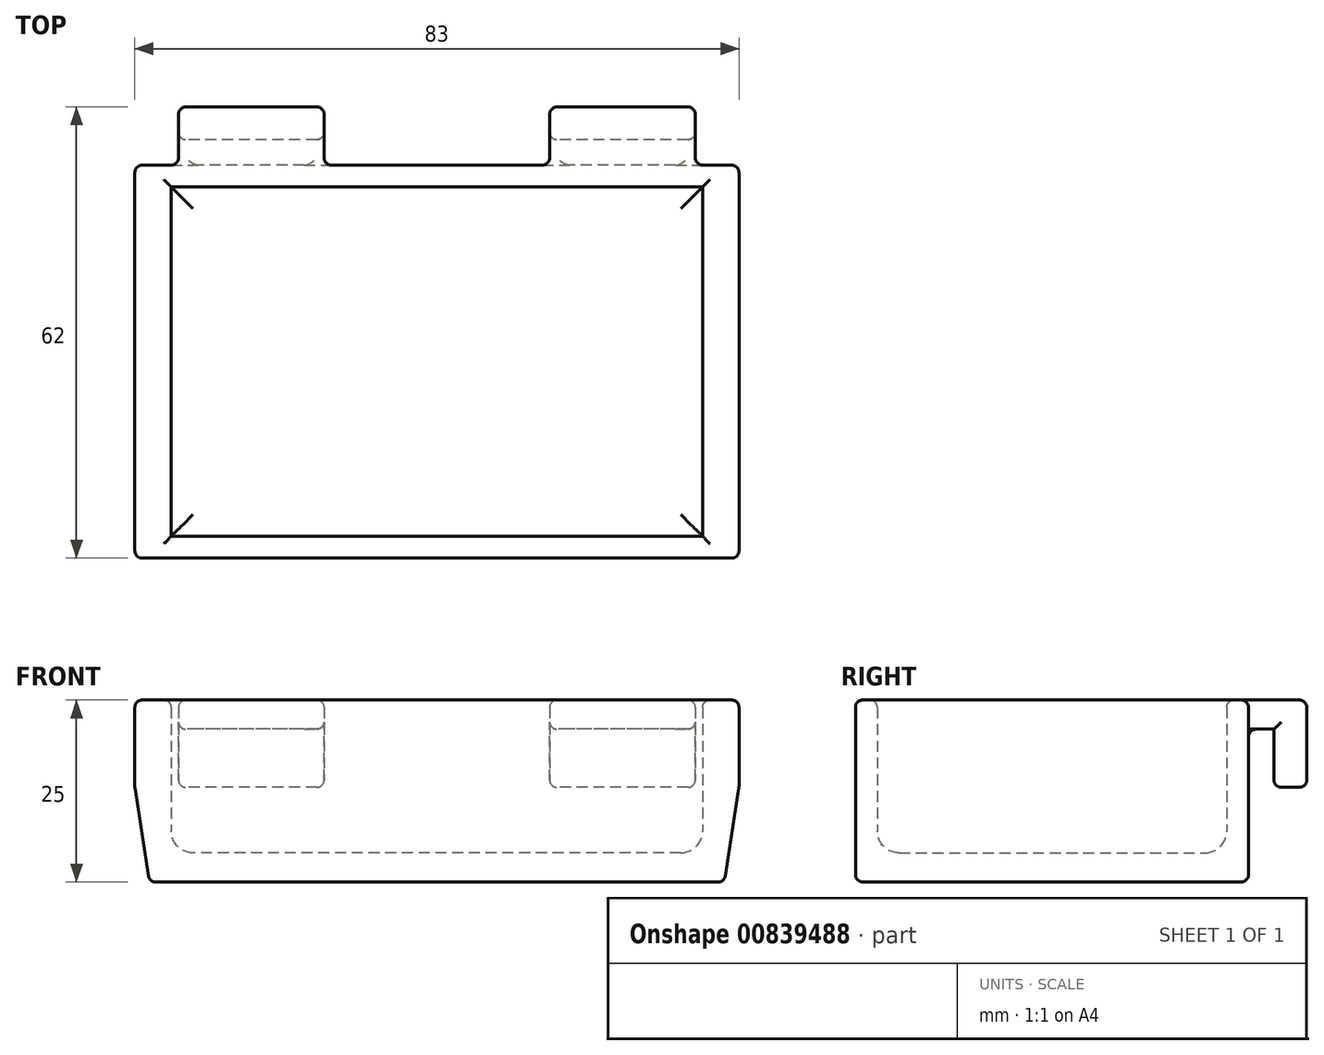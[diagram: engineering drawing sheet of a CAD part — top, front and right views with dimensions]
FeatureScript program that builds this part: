
annotation { "Feature Type Name" : "Feature", "Feature Type Description" : "" }
export const myFeature = defineFeature(function(context is Context, id is Id, definition is map)
    precondition{}
    {
        {
            var Q0;
            Q0=qCreatedBy(makeId("Top.planeOp"),FACE);
            var sketch = newSketch(context, id + "F0", { "sketchPlane" : qUnion([Q0])});
            skLineSegment(sketch, "E0.bottom", {"start": v(39.5, -27) * mm, "end": v(-39.5, -27) * mm});
            skLineSegment(sketch, "E0.top", {"start": v(39.5, 27) * mm, "end": v(-39.5, 27) * mm});
            skLineSegment(sketch, "E0.left", {"start": v(39.5, -27) * mm, "end": v(39.5, 27) * mm});
            skLineSegment(sketch, "E0.right", {"start": v(-39.5, -27) * mm, "end": v(-39.5, 27) * mm});
            skPoint(sketch, "E0.middle", {"position": v(0, 0) * mm});
            skLineSegment(sketch, "E1.bottom", {"start": v(36.5, -24) * mm, "end": v(-36.5, -24) * mm});
            skLineSegment(sketch, "E1.top", {"start": v(36.5, 24) * mm, "end": v(-36.5, 24) * mm});
            skLineSegment(sketch, "E1.left", {"start": v(36.5, -24) * mm, "end": v(36.5, 24) * mm});
            skLineSegment(sketch, "E1.right", {"start": v(-36.5, -24) * mm, "end": v(-36.5, 24) * mm});
            skSolve(sketch);
        }
        {
            var Q0;
            Q0=makeQuery(id+"F0.imprint","IMPRINT",FACE,{"disambiguationData":[TD([[makeQuery(id+"F0.imprint","IMPRINT",EDGE,{"derivedFrom":sQuery(id+"F0.wireOp",EDGE,"E1.bottom")}),-1.0]])]});
            extrude(context, id + "F1", {"entities" : qUnion([Q0]), "depth" : 4 * mm, "offsetDistance" : 25 * mm});
        }
        {
            var Q0;
            Q0=makeQuery(id+"F0.imprint","IMPRINT",FACE,{"disambiguationData":[TD([[makeQuery(id+"F0.imprint","IMPRINT",EDGE,{"derivedFrom":sQuery(id+"F0.wireOp",EDGE,"E0.bottom")}),-1.0]])]});
            extrude(context, id + "F2", {"entities" : qUnion([Q0]), "operationType" : NewBodyOperationType.ADD, "depth" : 25 * mm, "offsetDistance" : 25 * mm});
        }
        {
            var Q0;
            Q0=makeQuery(id+"F2.opExtrude","SWEPT_FACE",FACE,{"disambiguationData":[OSD([sQuery(id+"F0.wireOp",EDGE,"E0.bottom")])]});
            var sketch = newSketch(context, id + "F3", { "sketchPlane" : qUnion([Q0])});
            skLineSegment(sketch, "E2.bottom", {"start": v(-39.5, 0) * mm, "end": v(-41.5, 0) * mm});
            skLineSegment(sketch, "E2.top", {"start": v(-39.5, 25) * mm, "end": v(-41.5, 25) * mm});
            skLineSegment(sketch, "E2.left", {"start": v(-39.5, 0) * mm, "end": v(-39.5, 25) * mm});
            skLineSegment(sketch, "E2.right", {"start": v(-41.5, 0) * mm, "end": v(-41.5, 25) * mm});
            skLineSegment(sketch, "E3.bottom", {"start": v(39.5, 0) * mm, "end": v(41.5, 0) * mm});
            skLineSegment(sketch, "E3.top", {"start": v(39.5, 25) * mm, "end": v(41.5, 25) * mm});
            skLineSegment(sketch, "E3.left", {"start": v(39.5, 0) * mm, "end": v(39.5, 25) * mm});
            skLineSegment(sketch, "E3.right", {"start": v(41.5, 0) * mm, "end": v(41.5, 25) * mm});
            skLineSegment(sketch, "E4.bottom", {"start": v(-41.5, 25) * mm, "end": v(41.5, 25) * mm});
            skLineSegment(sketch, "E4.top", {"start": v(-41.5, 13) * mm, "end": v(41.5, 13) * mm});
            skLineSegment(sketch, "E4.left", {"start": v(-41.5, 25) * mm, "end": v(-41.5, 13) * mm});
            skLineSegment(sketch, "E4.right", {"start": v(41.5, 25) * mm, "end": v(41.5, 13) * mm});
            skLineSegment(sketch, "E5", {"start": v(-41.5, 13) * mm, "end": v(-39.5, 0) * mm});
            skLineSegment(sketch, "E6", {"start": v(39.5, 0) * mm, "end": v(41.5, 13) * mm});
            skSolve(sketch);
        }
        {
            var Q0;
            {var subQ0=sQuery(id+"F3.wireOp",EDGE,"E3.top");Q0=makeQuery(id+"F3.imprint","IMPRINT",FACE,{"disambiguationData":[TD([[makeQuery(id+"F3.imprint","IMPRINT",EDGE,{"derivedFrom":subQ0}),-1.0]])]});}
            var Q1;
            {var subQ0=sQuery(id+"F3.wireOp",EDGE,"E6");Q1=makeQuery(id+"F3.imprint","IMPRINT",FACE,{"disambiguationData":[TD([[makeQuery(id+"F3.imprint","IMPRINT",EDGE,{"derivedFrom":subQ0}),1.0]])]});}
            var Q2;
            {var subQ0=sQuery(id+"F3.wireOp",EDGE,"E2.top");Q2=makeQuery(id+"F3.imprint","IMPRINT",FACE,{"disambiguationData":[TD([[makeQuery(id+"F3.imprint","IMPRINT",EDGE,{"derivedFrom":subQ0}),1.0]])]});}
            var Q3;
            {var subQ0=sQuery(id+"F3.wireOp",EDGE,"E5");Q3=makeQuery(id+"F3.imprint","IMPRINT",FACE,{"disambiguationData":[TD([[makeQuery(id+"F3.imprint","IMPRINT",EDGE,{"derivedFrom":subQ0}),1.0]])]});}
            extrude(context, id + "F4", {"entities" : qUnion([Q0, Q1, Q2, Q3]), "operationType" : NewBodyOperationType.ADD, "oppositeDirection" : true, "depth" : 54 * mm, "offsetDistance" : 25 * mm});
        }
        {
            var Q0;
            Q0=makeQuery(id+"F4.boolean.opBoolean","MERGE",FACE,{"derivedFrom":[makeQuery(id+"F2.opExtrude","SWEPT_FACE",FACE,{"disambiguationData":[OSD([sQuery(id+"F0.wireOp",EDGE,"E0.top")])]}),makeQuery(id+"F4.opExtrude","CAP_FACE",FACE,{"disambiguationData":[OSD([sQuery(id+"F3.wireOp",EDGE,"E2.top"),sQuery(id+"F3.wireOp",EDGE,"E2.left"),sQuery(id+"F3.wireOp",EDGE,"E2.right"),sQuery(id+"F3.wireOp",EDGE,"E5")])],"isStart":false}),makeQuery(id+"F4.opExtrude","CAP_FACE",FACE,{"disambiguationData":[OSD([sQuery(id+"F3.wireOp",EDGE,"E3.top"),sQuery(id+"F3.wireOp",EDGE,"E3.left"),sQuery(id+"F3.wireOp",EDGE,"E3.right"),sQuery(id+"F3.wireOp",EDGE,"E6")])],"isStart":false})]});
            var sketch = newSketch(context, id + "F5", { "sketchPlane" : qUnion([Q0])});
            skLineSegment(sketch, "E7.bottom", {"start": v(-41.5, 25) * mm, "end": v(41.5, 25) * mm});
            skLineSegment(sketch, "E7.top", {"start": v(-41.5, 13) * mm, "end": v(41.5, 13) * mm});
            skLineSegment(sketch, "E7.left", {"start": v(-41.5, 25) * mm, "end": v(-41.5, 13) * mm});
            skLineSegment(sketch, "E7.right", {"start": v(41.5, 25) * mm, "end": v(41.5, 13) * mm});
            skLineSegment(sketch, "E8.bottom", {"start": v(-41.5, 25) * mm, "end": v(-35.5, 25) * mm});
            skLineSegment(sketch, "E8.top", {"start": v(-41.5, 13) * mm, "end": v(-35.5, 13) * mm});
            skLineSegment(sketch, "E8.right", {"start": v(-35.5, 25) * mm, "end": v(-35.5, 13) * mm});
            skLineSegment(sketch, "E9.bottom", {"start": v(41.5, 25) * mm, "end": v(35.5, 25) * mm});
            skLineSegment(sketch, "E9.top", {"start": v(41.5, 13) * mm, "end": v(35.5, 13) * mm});
            skLineSegment(sketch, "E9.right", {"start": v(35.5, 25) * mm, "end": v(35.5, 13) * mm});
            skLineSegment(sketch, "E10.bottom", {"start": v(-35.5, 25) * mm, "end": v(-15.5, 25) * mm});
            skLineSegment(sketch, "E10.top", {"start": v(-35.5, 13) * mm, "end": v(-15.5, 13) * mm});
            skLineSegment(sketch, "E10.right", {"start": v(-15.5, 25) * mm, "end": v(-15.5, 13) * mm});
            skLineSegment(sketch, "E11.bottom", {"start": v(35.5, 25) * mm, "end": v(15.5, 25) * mm});
            skLineSegment(sketch, "E11.top", {"start": v(35.5, 13) * mm, "end": v(15.5, 13) * mm});
            skLineSegment(sketch, "E11.right", {"start": v(15.5, 25) * mm, "end": v(15.5, 13) * mm});
            skSolve(sketch);
        }
        {
            var Q0;
            {var subQ0=sQuery(id+"F5.wireOp",EDGE,"E8.right");Q0=makeQuery(id+"F5.imprint","IMPRINT",FACE,{"disambiguationData":[TD([[makeQuery(id+"F5.imprint","IMPRINT",EDGE,{"derivedFrom":subQ0}),1.0]])]});}
            var Q1;
            {var subQ0=sQuery(id+"F5.wireOp",EDGE,"E9.right");Q1=makeQuery(id+"F5.imprint","IMPRINT",FACE,{"disambiguationData":[TD([[makeQuery(id+"F5.imprint","IMPRINT",EDGE,{"derivedFrom":subQ0}),-1.0]])]});}
            extrude(context, id + "F6", {"entities" : qUnion([Q0, Q1]), "operationType" : NewBodyOperationType.ADD, "depth" : 8 * mm, "offsetDistance" : 25 * mm});
        }
        {
            var Q0;
            Q0=makeQuery(id+"F6.opExtrude","SWEPT_FACE",FACE,{"disambiguationData":[OSD([sQuery(id+"F5.wireOp",EDGE,"E9.right")])]});
            var sketch = newSketch(context, id + "F7", { "sketchPlane" : qUnion([Q0])});
            skLineSegment(sketch, "E12.bottom", {"start": v(-27, 13) * mm, "end": v(-30.5, 13) * mm});
            skLineSegment(sketch, "E12.top", {"start": v(-27, 21) * mm, "end": v(-30.5, 21) * mm});
            skLineSegment(sketch, "E12.left", {"start": v(-27, 13) * mm, "end": v(-27, 21) * mm});
            skLineSegment(sketch, "E12.right", {"start": v(-30.5, 13) * mm, "end": v(-30.5, 21) * mm});
            skSolve(sketch);
        }
        {
            var Q0;
            Q0=makeQuery(id+"F7.imprint","IMPRINT",FACE,{"disambiguationData":[TD([[makeQuery(id+"F7.imprint","IMPRINT",EDGE,{"derivedFrom":sQuery(id+"F7.wireOp",EDGE,"E12.bottom")}),1.0]])]});
            extrude(context, id + "F8", {"entities" : qUnion([Q0]), "operationType" : NewBodyOperationType.REMOVE, "oppositeDirection" : true, "depth" : 80 * mm, "offsetDistance" : 25 * mm});
        }
        {
            var Q0;
            Q0=makeQuery(id+"F1.opExtrude","CAP_FACE",FACE,{"disambiguationData":[OSD([sQuery(id+"F0.wireOp",EDGE,"E1.bottom"),sQuery(id+"F0.wireOp",EDGE,"E1.top"),sQuery(id+"F0.wireOp",EDGE,"E1.left"),sQuery(id+"F0.wireOp",EDGE,"E1.right")])],"isStart":false});
            fillet(context, id + "F9", {"entities" : qUnion([Q0]), "radius" : 3 * mm, "tangentPropagation" : true, "allowEdgeOverflow" : false});
        }
        {
            var Q0;
            {var subQ0=sQuery(id+"F5.wireOp",EDGE,"E7.bottom");Q0=makeQuery(id+"F6.boolean.opBoolean","MERGE",FACE,{"derivedFrom":[makeQuery(id+"F4.boolean.opBoolean","MERGE",FACE,{"derivedFrom":[makeQuery(id+"F2.opExtrude","CAP_FACE",FACE,{"disambiguationData":[OSD([sQuery(id+"F0.wireOp",EDGE,"E0.bottom"),sQuery(id+"F0.wireOp",EDGE,"E0.top"),sQuery(id+"F0.wireOp",EDGE,"E0.left"),sQuery(id+"F0.wireOp",EDGE,"E0.right"),sQuery(id+"F0.wireOp",EDGE,"E1.bottom"),sQuery(id+"F0.wireOp",EDGE,"E1.top"),sQuery(id+"F0.wireOp",EDGE,"E1.left"),sQuery(id+"F0.wireOp",EDGE,"E1.right")])],"isStart":false}),makeQuery(id+"F4.opExtrude","SWEPT_FACE",FACE,{"disambiguationData":[OSD([sQuery(id+"F3.wireOp",EDGE,"E2.top")])]}),makeQuery(id+"F4.opExtrude","SWEPT_FACE",FACE,{"disambiguationData":[OSD([sQuery(id+"F3.wireOp",EDGE,"E3.top")])]})]}),makeQuery(id+"F6.opExtrude","SWEPT_FACE",FACE,{"disambiguationData":[OSD([subQ0]),TDD([makeQuery(id+"F5.imprint","IMPRINT",EDGE,{"disambiguationData":[TD([[makeQuery(id+"F5.imprint","INTERSECT",VERTEX,{"derivedFrom":[subQ0,sQuery(id+"F5.wireOp",EDGE,"E8.right")]}),-1.0]])],"derivedFrom":subQ0})])]}),makeQuery(id+"F6.opExtrude","SWEPT_FACE",FACE,{"disambiguationData":[OSD([subQ0]),TDD([makeQuery(id+"F5.imprint","IMPRINT",EDGE,{"disambiguationData":[TD([[makeQuery(id+"F5.imprint","INTERSECT",VERTEX,{"derivedFrom":[subQ0,sQuery(id+"F5.wireOp",EDGE,"E9.right")]}),1.0]])],"derivedFrom":subQ0})])]})]});}
            var Q1;
            {var subQ0=sQuery(id+"F0.wireOp",EDGE,"E1.right");var subQ1=sQuery(id+"F0.wireOp",EDGE,"E1.left");var subQ2=sQuery(id+"F0.wireOp",EDGE,"E1.top");var subQ3=sQuery(id+"F0.wireOp",EDGE,"E1.bottom");Q1=makeQuery(id+"F2.boolean.opBoolean","MERGE",FACE,{"derivedFrom":[makeQuery(id+"F1.opExtrude","CAP_FACE",FACE,{"disambiguationData":[OSD([subQ3,subQ2,subQ1,subQ0])],"isStart":true}),makeQuery(id+"F2.opExtrude","CAP_FACE",FACE,{"disambiguationData":[OSD([sQuery(id+"F0.wireOp",EDGE,"E0.bottom"),sQuery(id+"F0.wireOp",EDGE,"E0.top"),sQuery(id+"F0.wireOp",EDGE,"E0.left"),sQuery(id+"F0.wireOp",EDGE,"E0.right"),subQ3,subQ2,subQ1,subQ0])],"isStart":true})]});}
            var Q2;
            Q2=makeQuery(id+"F4.boolean.opBoolean","MERGE",FACE,{"derivedFrom":[makeQuery(id+"F2.opExtrude","SWEPT_FACE",FACE,{"disambiguationData":[OSD([sQuery(id+"F0.wireOp",EDGE,"E0.bottom")])]}),makeQuery(id+"F4.opExtrude","CAP_FACE",FACE,{"disambiguationData":[OSD([sQuery(id+"F3.wireOp",EDGE,"E2.top"),sQuery(id+"F3.wireOp",EDGE,"E2.left"),sQuery(id+"F3.wireOp",EDGE,"E2.right"),sQuery(id+"F3.wireOp",EDGE,"E5")])],"isStart":true}),makeQuery(id+"F4.opExtrude","CAP_FACE",FACE,{"disambiguationData":[OSD([sQuery(id+"F3.wireOp",EDGE,"E3.top"),sQuery(id+"F3.wireOp",EDGE,"E3.left"),sQuery(id+"F3.wireOp",EDGE,"E3.right"),sQuery(id+"F3.wireOp",EDGE,"E6")])],"isStart":true})]});
            var Q3;
            Q3=makeQuery(id+"F4.opExtrude","SWEPT_FACE",FACE,{"disambiguationData":[OSD([sQuery(id+"F3.wireOp",EDGE,"E6")])]});
            var Q4;
            Q4=makeQuery(id+"F4.opExtrude","SWEPT_FACE",FACE,{"disambiguationData":[OSD([sQuery(id+"F3.wireOp",EDGE,"E3.right")])]});
            var Q5;
            Q5=makeQuery(id+"F4.opExtrude","SWEPT_FACE",FACE,{"disambiguationData":[OSD([sQuery(id+"F3.wireOp",EDGE,"E5")])]});
            var Q6;
            Q6=makeQuery(id+"F4.opExtrude","SWEPT_FACE",FACE,{"disambiguationData":[OSD([sQuery(id+"F3.wireOp",EDGE,"E2.right")])]});
            var Q7;
            Q7=makeQuery(id+"F6.opExtrude","CAP_FACE",FACE,{"disambiguationData":[OSD([sQuery(id+"F5.wireOp",EDGE,"E7.bottom"),sQuery(id+"F5.wireOp",EDGE,"E7.top"),sQuery(id+"F5.wireOp",EDGE,"E9.right"),sQuery(id+"F5.wireOp",EDGE,"E11.right")])],"isStart":false});
            var Q8;
            Q8=makeQuery(id+"F6.opExtrude","CAP_FACE",FACE,{"disambiguationData":[OSD([sQuery(id+"F5.wireOp",EDGE,"E7.bottom"),sQuery(id+"F5.wireOp",EDGE,"E7.top"),sQuery(id+"F5.wireOp",EDGE,"E8.right"),sQuery(id+"F5.wireOp",EDGE,"E10.right")])],"isStart":false});
            var Q9;
            {var subQ0=sQuery(id+"F5.wireOp",EDGE,"E7.top");Q9=makeQuery(id+"F6.opExtrude","SWEPT_FACE",FACE,{"disambiguationData":[OSD([subQ0]),TDD([makeQuery(id+"F5.imprint","IMPRINT",EDGE,{"disambiguationData":[TD([[makeQuery(id+"F5.imprint","INTERSECT",VERTEX,{"derivedFrom":[subQ0,sQuery(id+"F5.wireOp",EDGE,"E10.right")]}),1.0]])],"derivedFrom":subQ0})])]});}
            var Q10;
            {var subQ0=sQuery(id+"F5.wireOp",EDGE,"E7.top");Q10=makeQuery(id+"F6.opExtrude","SWEPT_FACE",FACE,{"disambiguationData":[OSD([subQ0]),TDD([makeQuery(id+"F5.imprint","IMPRINT",EDGE,{"disambiguationData":[TD([[makeQuery(id+"F5.imprint","INTERSECT",VERTEX,{"derivedFrom":[subQ0,sQuery(id+"F5.wireOp",EDGE,"E9.right")]}),1.0]])],"derivedFrom":subQ0})])]});}
            var Q11;
            Q11=makeQuery(id+"F6.opExtrude","SWEPT_FACE",FACE,{"disambiguationData":[OSD([sQuery(id+"F5.wireOp",EDGE,"E11.right")])]});
            var Q12;
            Q12=makeQuery(id+"F6.opExtrude","SWEPT_FACE",FACE,{"disambiguationData":[OSD([sQuery(id+"F5.wireOp",EDGE,"E8.right")])]});
            var Q13;
            Q13=makeQuery(id+"F6.opExtrude","SWEPT_FACE",FACE,{"disambiguationData":[OSD([sQuery(id+"F5.wireOp",EDGE,"E10.right")])]});
            var Q14;
            Q14=makeQuery(id+"F6.opExtrude","SWEPT_FACE",FACE,{"disambiguationData":[OSD([sQuery(id+"F5.wireOp",EDGE,"E9.right")])]});
            fillet(context, id + "F10", {"entities" : qUnion([Q0, Q1, Q2, Q3, Q4, Q5, Q6, Q7, Q8, Q9, Q10, Q11, Q12, Q13, Q14]), "radius" : 1 * mm, "tangentPropagation" : true, "allowEdgeOverflow" : false});
        }
    });
